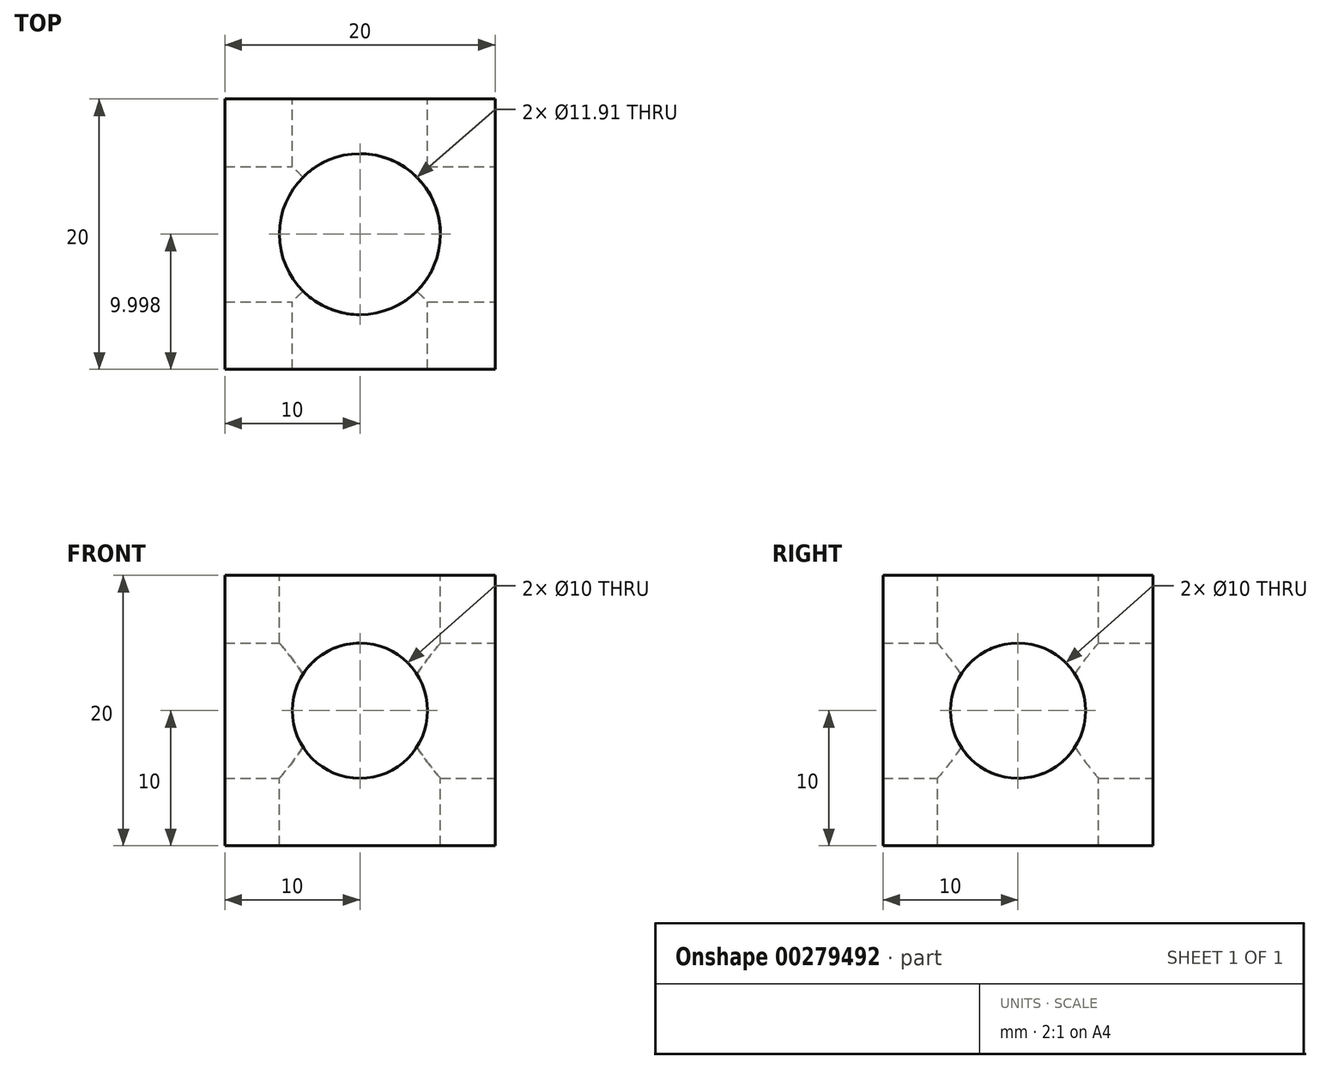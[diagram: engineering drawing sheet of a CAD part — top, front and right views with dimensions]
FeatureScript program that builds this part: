
annotation { "Feature Type Name" : "Feature", "Feature Type Description" : "" }
export const myFeature = defineFeature(function(context is Context, id is Id, definition is map)
    precondition{}
    {
        {
            var Q0;
            Q0=qCreatedBy(makeId("Top.planeOp"),FACE);
            var sketch = newSketch(context, id + "F0", { "sketchPlane" : qUnion([Q0])});
            skLineSegment(sketch, "E0.bottom", {"start": v(0, 20) * mm, "end": v(20, 20) * mm});
            skLineSegment(sketch, "E0.top", {"start": v(0, 0) * mm, "end": v(20, 0) * mm});
            skLineSegment(sketch, "E0.left", {"start": v(0, 20) * mm, "end": v(0, 0) * mm});
            skLineSegment(sketch, "E0.right", {"start": v(20, 20) * mm, "end": v(20, 0) * mm});
            skSolve(sketch);
        }
        {
            var Q0;
            Q0=makeQuery(id+"F0.imprint","IMPRINT",FACE,{"disambiguationData":[TD([[makeQuery(id+"F0.imprint","IMPRINT",EDGE,{"derivedFrom":sQuery(id+"F0.wireOp",EDGE,"E0.bottom")}),-1.0]])]});
            extrude(context, id + "F1", {"entities" : qUnion([Q0]), "depth" : 20 * mm});
        }
        {
            var Q0;
            Q0=makeQuery(id+"F1.opExtrude","CAP_FACE",FACE,{"disambiguationData":[OSD([sQuery(id+"F0.wireOp",EDGE,"E0.bottom"),sQuery(id+"F0.wireOp",EDGE,"E0.top"),sQuery(id+"F0.wireOp",EDGE,"E0.left"),sQuery(id+"F0.wireOp",EDGE,"E0.right")])],"isStart":false});
            var sketch = newSketch(context, id + "F2", { "sketchPlane" : qUnion([Q0])});
            skCircle(sketch, "E1", {"center": v(10, 10) * mm, "radius": 5.96 * mm});
            skLineSegment(sketch, "E2", {"start": v(0, 10) * mm, "end": v(20, 10) * mm});
            skSolve(sketch);
        }
        {
            var Q0;
            Q0=makeQuery(id+"F2.imprint","IMPRINT",FACE,{"disambiguationData":[TD([[makeQuery(id+"F2.imprint","IMPRINT",EDGE,{"derivedFrom":sQuery(id+"F2.wireOp",EDGE,"E1")}),1.0]])]});
            extrude(context, id + "F3", {"entities" : qUnion([Q0]), "operationType" : NewBodyOperationType.REMOVE, "oppositeDirection" : true, "depth" : 20 * mm});
        }
        {
            var Q0;
            Q0=makeQuery(id+"F1.opExtrude","SWEPT_FACE",FACE,{"disambiguationData":[OSD([sQuery(id+"F0.wireOp",EDGE,"E0.bottom")])]});
            var sketch = newSketch(context, id + "F4", { "sketchPlane" : qUnion([Q0])});
            skCircle(sketch, "E3", {"center": v(-10, 10) * mm, "radius": 5 * mm});
            skLineSegment(sketch, "E4", {"start": v(-20, 10) * mm, "end": v(0, 10) * mm});
            skSolve(sketch);
        }
        {
            var Q0;
            Q0 = qSketchRegion(id + "F4", true);
            extrude(context, id + "F5", {"entities" : qUnion([Q0]), "operationType" : NewBodyOperationType.REMOVE, "oppositeDirection" : true, "depth" : 20 * mm});
        }
        {
            var Q0;
            Q0=makeQuery(id+"F1.opExtrude","SWEPT_FACE",FACE,{"disambiguationData":[OSD([sQuery(id+"F0.wireOp",EDGE,"E0.right")])]});
            var sketch = newSketch(context, id + "F6", { "sketchPlane" : qUnion([Q0])});
            skCircle(sketch, "E5", {"center": v(10, 10) * mm, "radius": 5 * mm});
            skSolve(sketch);
        }
        {
            var Q0;
            Q0 = qSketchRegion(id + "F6", true);
            extrude(context, id + "F7", {"entities" : qUnion([Q0]), "operationType" : NewBodyOperationType.REMOVE, "oppositeDirection" : true, "depth" : 20 * mm});
        }
    });
